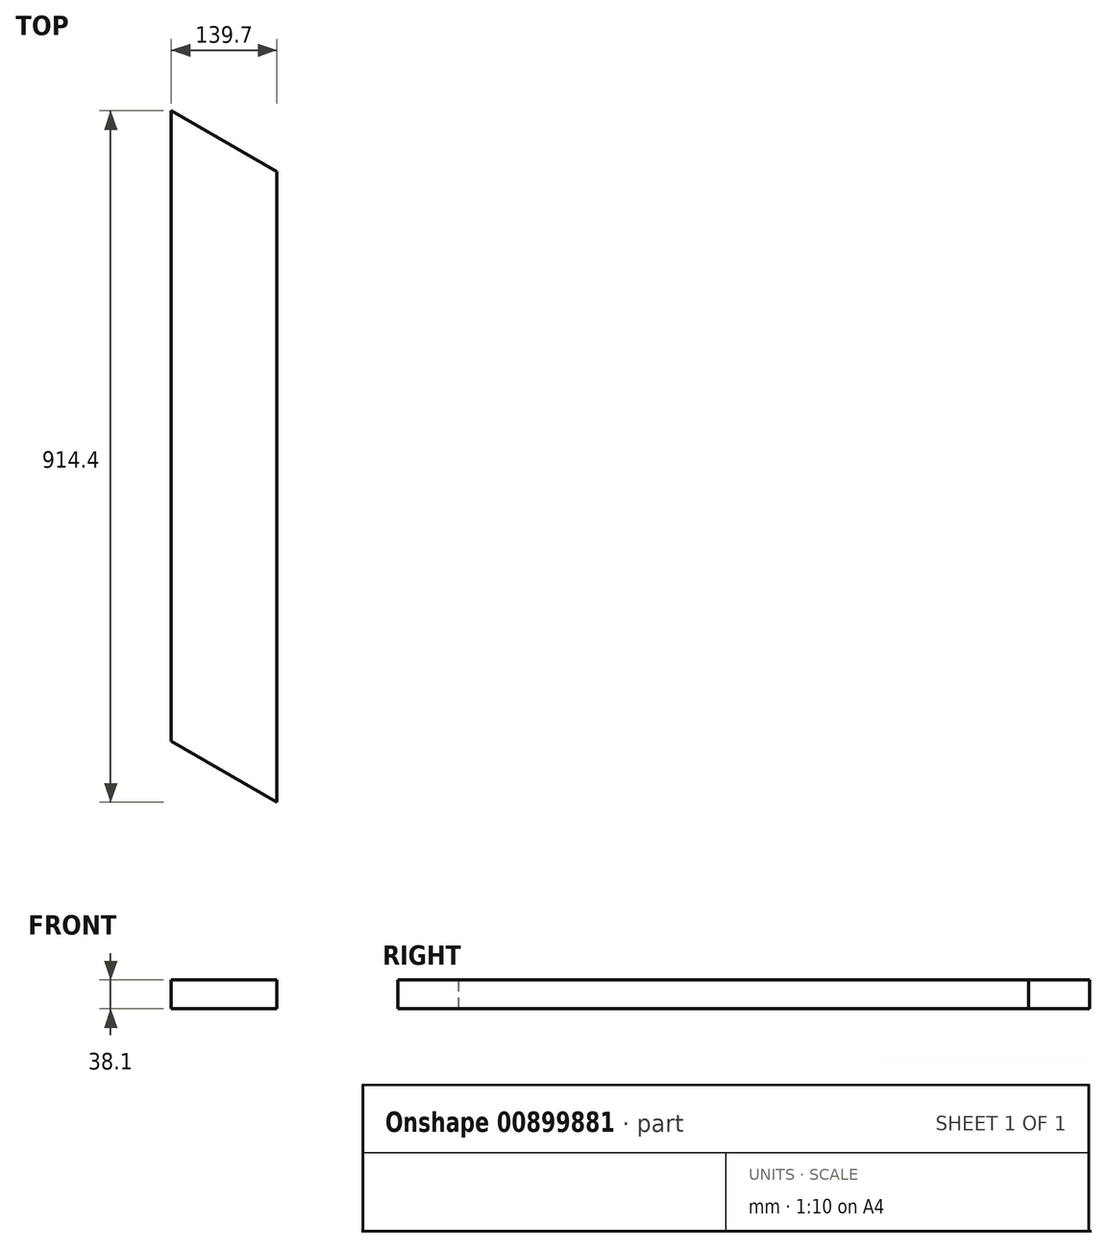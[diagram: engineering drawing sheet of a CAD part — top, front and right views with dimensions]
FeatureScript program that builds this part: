
annotation { "Feature Type Name" : "Feature", "Feature Type Description" : "" }
export const myFeature = defineFeature(function(context is Context, id is Id, definition is map)
    precondition{}
    {
        {
            var Q0;
            Q0=qCreatedBy(makeId("Front.planeOp"),FACE);
            var sketch = newSketch(context, id + "F0", { "sketchPlane" : qUnion([Q0])});
            skLineSegment(sketch, "E0.bottom", {"start": v(0, 0) * mm, "end": v(139.7, 0) * mm});
            skLineSegment(sketch, "E0.top", {"start": v(0, 38.1) * mm, "end": v(139.7, 38.1) * mm});
            skLineSegment(sketch, "E0.left", {"start": v(0, 0) * mm, "end": v(0, 38.1) * mm});
            skLineSegment(sketch, "E0.right", {"start": v(139.7, 0) * mm, "end": v(139.7, 38.1) * mm});
            skSolve(sketch);
        }
        {
            var Q0;
            Q0 = qSketchRegion(id + "F0", true);
            extrude(context, id + "F1", {"entities" : qUnion([Q0]), "depth" : 914.4 * mm, "offsetDistance" : 25.4 * mm});
        }
        {
            var Q0;
            Q0=qCreatedBy(makeId("Top.planeOp"),FACE);
            var sketch = newSketch(context, id + "F2", { "sketchPlane" : qUnion([Q0])});
            skLineSegment(sketch, "E1", {"start": v(0, 0) * mm, "end": v(152.4, -87.99) * mm});
            skLineSegment(sketch, "E2", {"start": v(152.4, -87.99) * mm, "end": v(152.4, 0) * mm});
            skLineSegment(sketch, "E3", {"start": v(152.4, 0) * mm, "end": v(0, 0) * mm});
            skSolve(sketch);
        }
        {
            var Q0;
            Q0 = qSketchRegion(id + "F2", true);
            extrude(context, id + "F3", {"entities" : qUnion([Q0]), "operationType" : NewBodyOperationType.REMOVE, "depth" : 50.8 * mm, "offsetDistance" : 25.4 * mm});
        }
        {
            var Q0;
            Q0=qCreatedBy(makeId("Top.planeOp"),FACE);
            var sketch = newSketch(context, id + "F4", { "sketchPlane" : qUnion([Q0])});
            skLineSegment(sketch, "E4", {"start": v(-12.7, -826.41) * mm, "end": v(-12.7, -914.4) * mm});
            skLineSegment(sketch, "E5", {"start": v(-12.7, -914.4) * mm, "end": v(139.7, -914.4) * mm});
            skLineSegment(sketch, "E6", {"start": v(139.7, -914.4) * mm, "end": v(-12.7, -826.41) * mm});
            skSolve(sketch);
        }
        {
            var Q0;
            Q0 = qSketchRegion(id + "F4", true);
            extrude(context, id + "F5", {"entities" : qUnion([Q0]), "operationType" : NewBodyOperationType.REMOVE, "depth" : 50.8 * mm, "offsetDistance" : 25.4 * mm});
        }
    });
